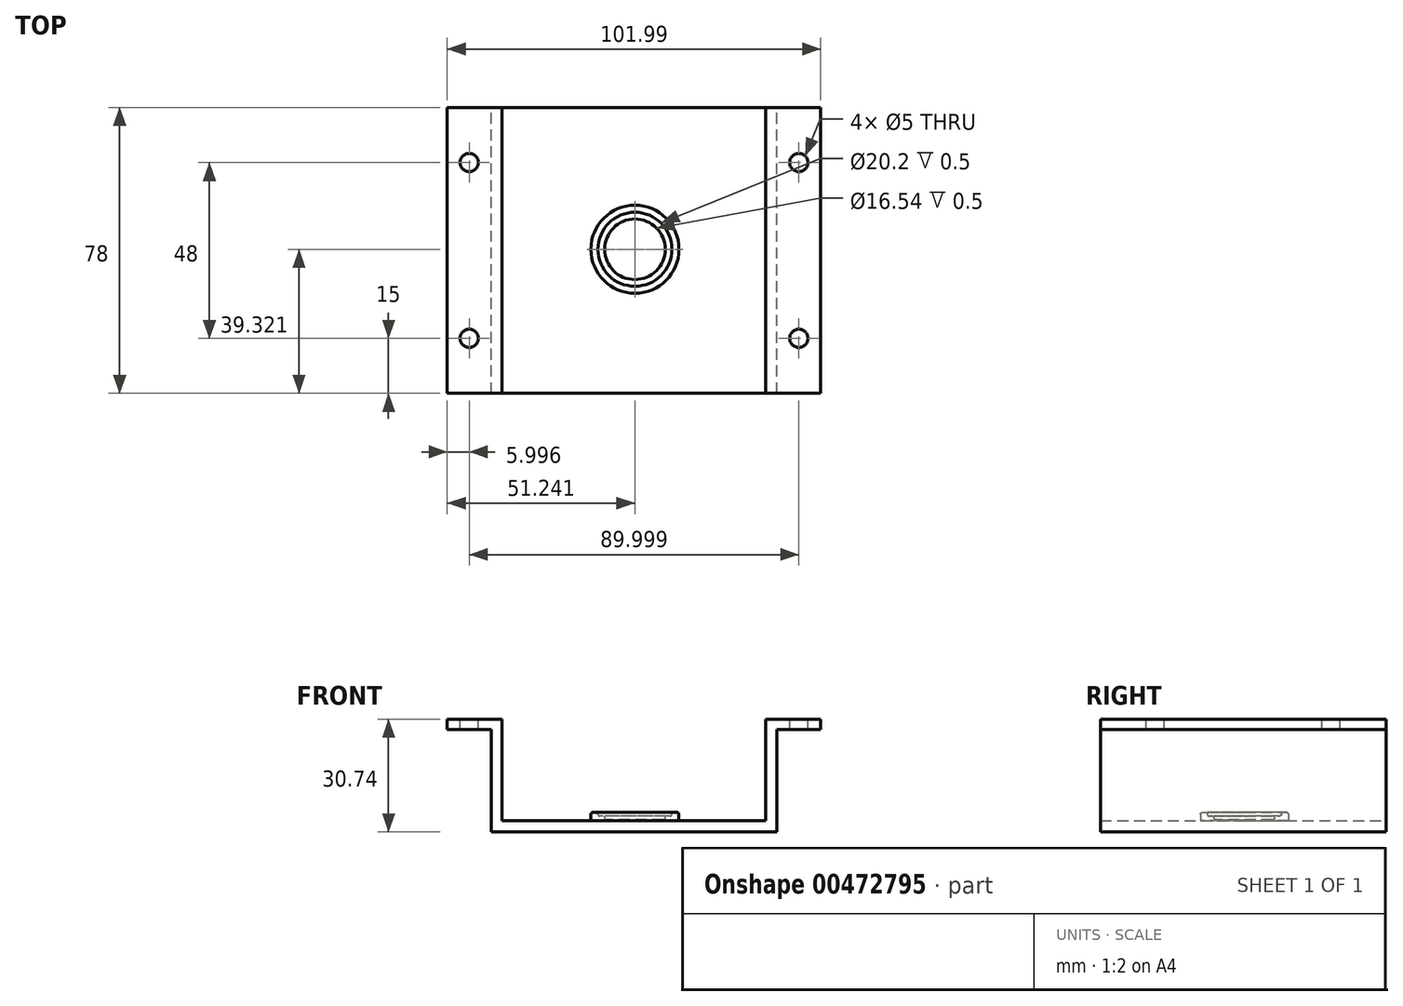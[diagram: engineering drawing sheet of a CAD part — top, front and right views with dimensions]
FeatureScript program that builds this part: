
annotation { "Feature Type Name" : "Feature", "Feature Type Description" : "" }
export const myFeature = defineFeature(function(context is Context, id is Id, definition is map)
    precondition{}
    {
        {
            var Q0;
            Q0=qCreatedBy(makeId("Front.planeOp"),FACE);
            var sketch = newSketch(context, id + "F0", { "sketchPlane" : qUnion([Q0])});
            skLineSegment(sketch, "E0", {"start": v(-2.97, -6.62) * mm, "end": v(-2.97, -9.62) * mm});
            skLineSegment(sketch, "E1", {"start": v(-2.97, -9.62) * mm, "end": v(36.03, -9.62) * mm});
            skLineSegment(sketch, "E2", {"start": v(36.03, -9.62) * mm, "end": v(36.03, 18.38) * mm});
            skLineSegment(sketch, "E3", {"start": v(36.03, 18.38) * mm, "end": v(48.02, 18.38) * mm});
            skLineSegment(sketch, "E4", {"start": v(48.02, 18.38) * mm, "end": v(48.02, 21.12) * mm});
            skLineSegment(sketch, "E5", {"start": v(48.02, 21.12) * mm, "end": v(33.02, 21.12) * mm});
            skLineSegment(sketch, "E6", {"start": v(33.02, 21.12) * mm, "end": v(33.02, -6.62) * mm});
            skLineSegment(sketch, "E7", {"start": v(33.02, -6.62) * mm, "end": v(-2.97, -6.62) * mm});
            skLineSegment(sketch, "E8.MirrorCS", {"start": v(-53.97, 18.38) * mm, "end": v(-53.97, 21.12) * mm});
            skLineSegment(sketch, "E9.MirrorCS", {"start": v(-41.97, -9.62) * mm, "end": v(-41.97, 18.38) * mm});
            skLineSegment(sketch, "E10.MirrorCS", {"start": v(-41.97, 18.38) * mm, "end": v(-53.97, 18.38) * mm});
            skLineSegment(sketch, "E11.MirrorCS", {"start": v(-53.97, 21.12) * mm, "end": v(-38.97, 21.12) * mm});
            skLineSegment(sketch, "E12.MirrorCS", {"start": v(-38.97, 21.12) * mm, "end": v(-38.97, -6.62) * mm});
            skLineSegment(sketch, "E13.MirrorCS", {"start": v(-2.97, -9.62) * mm, "end": v(-41.97, -9.62) * mm});
            skLineSegment(sketch, "E14.MirrorCS", {"start": v(-38.97, -6.62) * mm, "end": v(-2.97, -6.62) * mm});
            skPoint(sketch, "E15.MirrorCS.start.orphan", {"position": v(36.03, 18.38) * mm});
            skSolve(sketch);
        }
        {
            var Q0;
            Q0=qSketchRegion(id+"F0",true);
            extrude(context, id + "F1", {"entities" : qUnion([Q0]), "endBound" : BoundingType.SYMMETRIC, "depth" : 78 * mm});
        }
        {
            var Q0;
            Q0=makeQuery(id+"F1.opExtrude","SWEPT_FACE",FACE,{"disambiguationData":[OSD([sQuery(id+"F0.wireOp",EDGE,"E5")])]});
            var sketch = newSketch(context, id + "F2", { "sketchPlane" : qUnion([Q0])});
            skLineSegment(sketch, "E16", {"start": v(42.02, -39) * mm, "end": v(42.02, 39) * mm, "construction": true});
            skLineSegment(sketch, "E17.0.0", {"start": v(-38.97, 39) * mm, "end": v(-53.97, 39) * mm, "construction": true});
            skLineSegment(sketch, "E17.0.1", {"start": v(-53.97, 39) * mm, "end": v(-53.97, -39) * mm, "construction": true});
            skLineSegment(sketch, "E17.0.2", {"start": v(-53.97, -39) * mm, "end": v(-38.97, -39) * mm, "construction": true});
            skLineSegment(sketch, "E17.0.3", {"start": v(-38.97, -39) * mm, "end": v(-38.97, 39) * mm, "construction": true});
            skLineSegment(sketch, "E18", {"start": v(-47.97, 39) * mm, "end": v(-47.97, -39) * mm, "construction": true});
            skLineSegment(sketch, "E19", {"start": v(-53.97, -24) * mm, "end": v(48.02, -24) * mm, "construction": true});
            skLineSegment(sketch, "E20", {"start": v(48.02, 24) * mm, "end": v(-53.97, 24) * mm, "construction": true});
            skLineSegment(sketch, "E21", {"start": v(48.02, -24) * mm, "end": v(48.02, -39) * mm, "construction": true});
            skLineSegment(sketch, "E22", {"start": v(48.02, 39) * mm, "end": v(48.02, 24) * mm, "construction": true});
            skCircle(sketch, "E23", {"center": v(42.02, -24) * mm, "radius": 2.5 * mm});
            skCircle(sketch, "E24", {"center": v(42.02, 24) * mm, "radius": 2.5 * mm});
            skCircle(sketch, "E25", {"center": v(-47.97, 24) * mm, "radius": 2.5 * mm});
            skCircle(sketch, "E26", {"center": v(-47.97, -24) * mm, "radius": 2.5 * mm});
            skSolve(sketch);
        }
        {
            var Q0;
            Q0=qSketchRegion(id+"F2",true);
            extrude(context, id + "F3", {"entities" : qUnion([Q0]), "operationType" : NewBodyOperationType.REMOVE, "endBound" : BoundingType.UP_TO_NEXT, "oppositeDirection" : true, "depth" : 25 * mm});
        }
        {
            var Q0;
            Q0=makeQuery(id+"F1.opExtrude","SWEPT_FACE",FACE,{"disambiguationData":[OSD([sQuery(id+"F0.wireOp",EDGE,"E1"),sQuery(id+"F0.wireOp",EDGE,"E13.MirrorCS")])]});
            var sketch = newSketch(context, id + "F4", { "sketchPlane" : qUnion([Q0])});
            skCircle(sketch, "E27", {"center": v(-2.73, -0.32) * mm, "radius": 12.02 * mm});
            skSolve(sketch);
        }
        {
            var Q0;
            Q0 = qSketchRegion(id + "F4", true);
            extrude(context, id + "F5", {"entities" : qUnion([Q0]), "operationType" : NewBodyOperationType.ADD, "oppositeDirection" : true, "depth" : 5.3 * mm});
        }
        {
            var Q0;
            Q0=makeQuery(id+"F5.opExtrude","CAP_FACE",FACE,{"disambiguationData":[OSD([sQuery(id+"F4.wireOp",EDGE,"E27")])],"isStart":false});
            var sketch = newSketch(context, id + "F6", { "sketchPlane" : qUnion([Q0])});
            skCircle(sketch, "E28", {"center": v(-2.73, 0.32) * mm, "radius": 10.1 * mm});
            skSolve(sketch);
        }
        {
            var Q0;
            Q0 = qSketchRegion(id + "F6", true);
            extrude(context, id + "F7", {"entities" : qUnion([Q0]), "operationType" : NewBodyOperationType.REMOVE, "oppositeDirection" : true, "depth" : 1 * mm});
        }
        {
            var Q0;
            Q0=makeQuery(id+"F7.boolean.opBoolean","COPY",FACE,{"derivedFrom":makeQuery(id+"F7.opExtrude","CAP_FACE",FACE,{"disambiguationData":[OSD([sQuery(id+"F6.wireOp",EDGE,"E28")])],"isStart":false})});
            var sketch = newSketch(context, id + "F8", { "sketchPlane" : qUnion([Q0])});
            skCircle(sketch, "E29", {"center": v(-2.73, 0.32) * mm, "radius": 8.27 * mm});
            skSolve(sketch);
        }
        {
            var Q0;
            Q0 = qSketchRegion(id + "F8", true);
            extrude(context, id + "F9", {"entities" : qUnion([Q0]), "operationType" : NewBodyOperationType.REMOVE, "oppositeDirection" : true, "depth" : 1 * mm});
        }
        {
            var Q0;
            Q0=makeQuery(id+"F5.opExtrude","CAP_EDGE",EDGE,{"disambiguationData":[OSD([sQuery(id+"F4.wireOp",EDGE,"E27")])],"isStart":false});
            var Q1;
            Q1=makeQuery(id+"F7.boolean.opBoolean","COPY",EDGE,{"derivedFrom":makeQuery(id+"F7.opExtrude","CAP_EDGE",EDGE,{"disambiguationData":[OSD([sQuery(id+"F6.wireOp",EDGE,"E28")])],"isStart":true})});
            var Q2;
            Q2=makeQuery(id+"F7.boolean.opBoolean","COPY",EDGE,{"derivedFrom":makeQuery(id+"F7.opExtrude","CAP_EDGE",EDGE,{"disambiguationData":[OSD([sQuery(id+"F6.wireOp",EDGE,"E28")])],"isStart":false})});
            var Q3;
            Q3=makeQuery(id+"F9.boolean.opBoolean","COPY",EDGE,{"derivedFrom":makeQuery(id+"F9.opExtrude","CAP_EDGE",EDGE,{"disambiguationData":[OSD([sQuery(id+"F8.wireOp",EDGE,"E29")])],"isStart":true})});
            var Q4;
            Q4=makeQuery(id+"F9.boolean.opBoolean","COPY",EDGE,{"derivedFrom":makeQuery(id+"F9.opExtrude","CAP_EDGE",EDGE,{"disambiguationData":[OSD([sQuery(id+"F8.wireOp",EDGE,"E29")])],"isStart":false})});
            fillet(context, id + "F10", {"entities" : qUnion([Q0, Q1, Q2, Q3, Q4]), "radius" : 0.5 * mm, "allowEdgeOverflow" : false});
        }
    });
